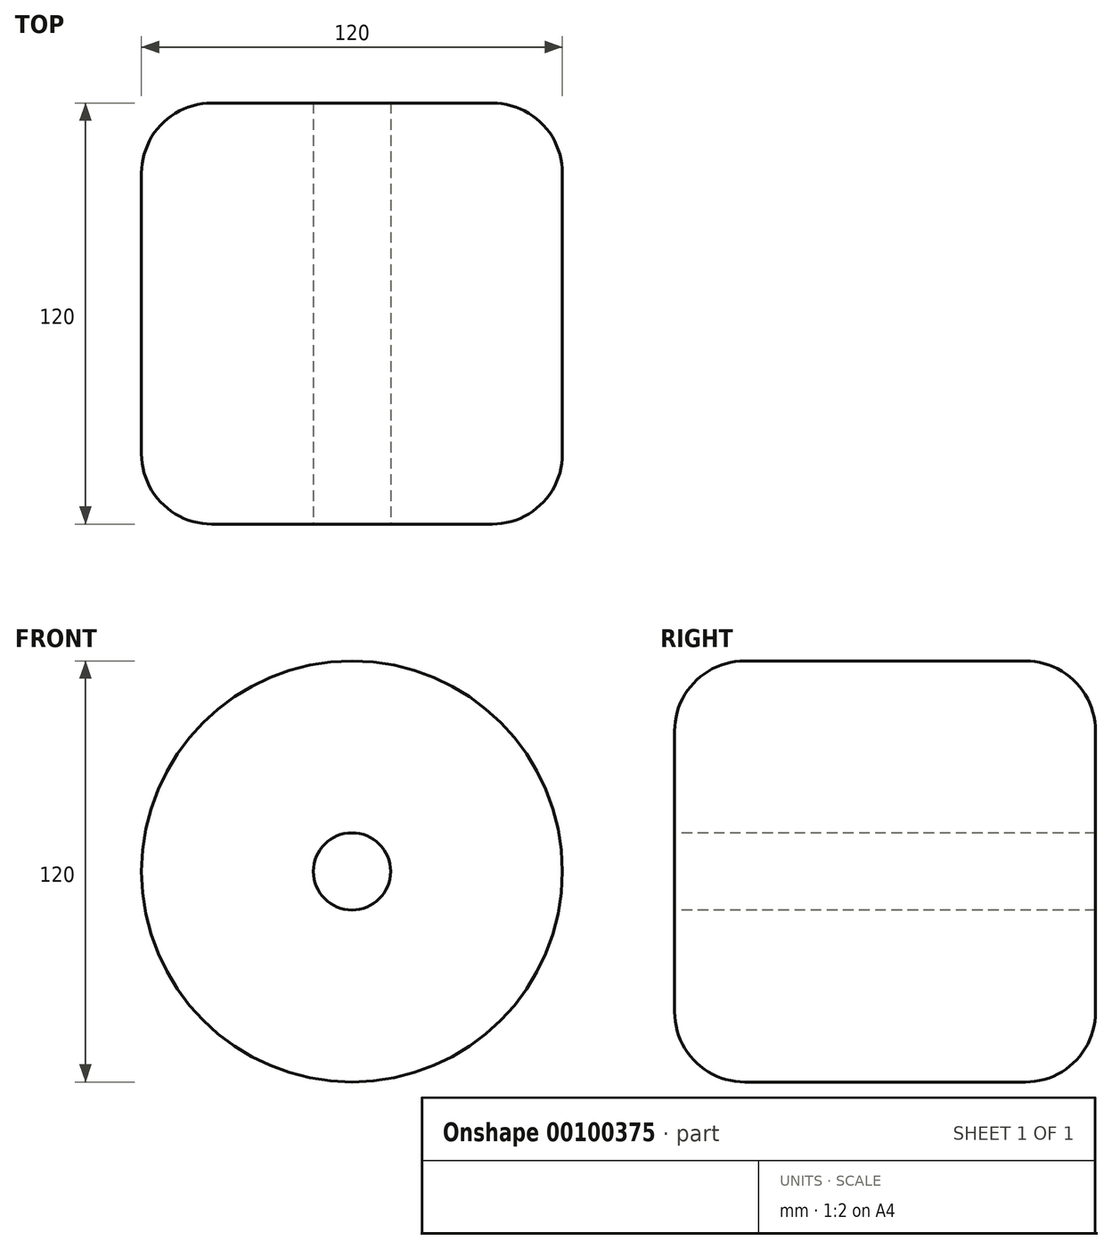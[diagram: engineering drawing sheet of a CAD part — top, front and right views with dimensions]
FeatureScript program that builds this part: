
annotation { "Feature Type Name" : "Feature", "Feature Type Description" : "" }
export const myFeature = defineFeature(function(context is Context, id is Id, definition is map)
    precondition{}
    {
        {
            var Q0;
            Q0=qCreatedBy(makeId("Front.planeOp"),FACE);
            var sketch = newSketch(context, id + "F0", { "sketchPlane" : qUnion([Q0])});
            skCircle(sketch, "E0", {"center": v(0, 0) * mm, "radius": 60 * mm});
            skSolve(sketch);
        }
        {
            var Q0;
            Q0 = qSketchRegion(id + "F0", true);
            extrude(context, id + "F1", {"entities" : qUnion([Q0]), "depth" : 120 * mm});
        }
        {
            var Q0;
            Q0=makeQuery(id+"F1.opExtrude","CAP_FACE",FACE,{"disambiguationData":[OSD([sQuery(id+"F0.wireOp",EDGE,"E0")])],"isStart":false});
            var sketch = newSketch(context, id + "F2", { "sketchPlane" : qUnion([Q0])});
            skPoint(sketch, "E1", {"position": v(0, 0) * mm});
            skSolve(sketch);
        }
        {
            var Q0;
            Q0=sQuery(id+"F2.wireOp",VERTEX,"E1");
            var Q1;
            Q1=makeQuery(id+"F1.opExtrude","SWEPT_BODY",BODY,{"disambiguationData":[OSD([sQuery(id+"F0.wireOp",EDGE,"E0")])]});
            hole(context, id + "F3", {"style" : HoleStyle.SIMPLE, "endStyle" : HoleEndStyle.THROUGH, "standardTappedOrClearance" : lookupTablePath({ "standard" : "ISO", "fit" : "Normal", "size" : "M20", "type" : "Clearance" }), "standardBlindInLast" : lookupTablePath({ "fit" : "Standard", "standard" : "ISO", "size" : "M20", "type" : "Clearance" }), "holeDiameter" : 22 * mm, "locations" : qUnion([Q0]), "scope" : qUnion([Q1]), "isTappedThrough" : true});
        }
        {
            var Q0;
            Q0=makeQuery(id+"F1.opExtrude","SWEPT_FACE",FACE,{"disambiguationData":[OSD([sQuery(id+"F0.wireOp",EDGE,"E0")])]});
            var Q1;
            Q1=makeQuery(id+"F3.hole-0.boolean.opBoolean","COPY",FACE,{"derivedFrom":makeQuery(id+"F3.hole-0.opRevolve","SWEPT_FACE",FACE,{"disambiguationData":[OSD([sQuery(id+"F3.hole-0.sketch.wireOp",EDGE,"core_line_2")])]})});
            fillet(context, id + "F4", {"entities" : qUnion([Q0, Q1]), "radius" : 20 * mm, "tangentPropagation" : true, "allowEdgeOverflow" : false});
        }
    });
